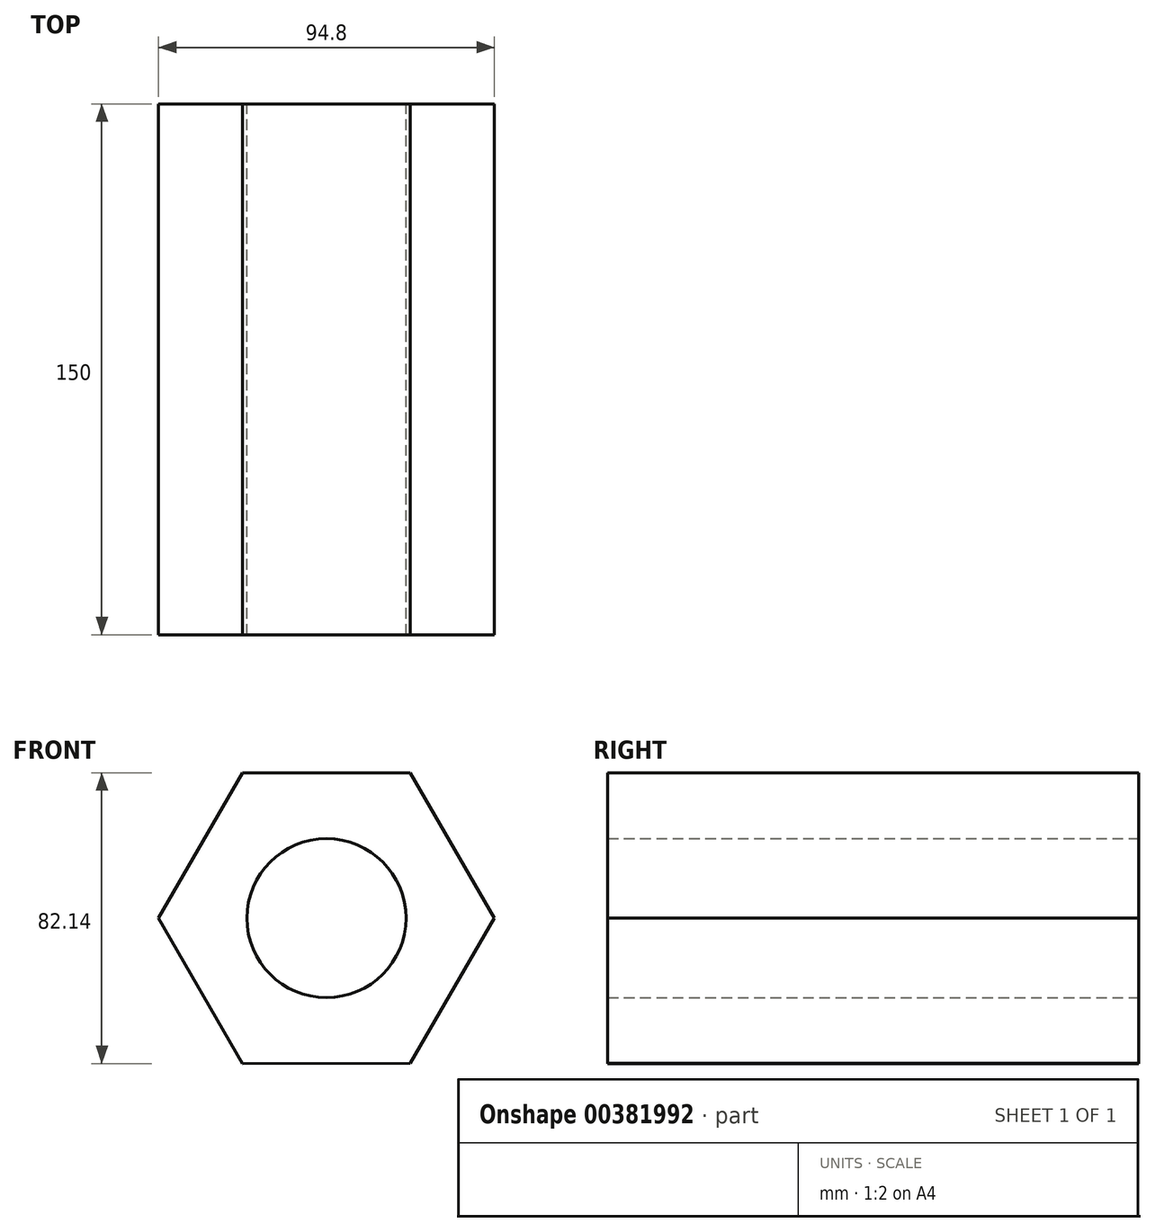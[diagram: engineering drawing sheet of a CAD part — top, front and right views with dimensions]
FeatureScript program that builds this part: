
annotation { "Feature Type Name" : "Feature", "Feature Type Description" : "" }
export const myFeature = defineFeature(function(context is Context, id is Id, definition is map)
    precondition{}
    {
        {
            var Q0;
            Q0=qCreatedBy(makeId("Front.planeOp"),FACE);
            var sketch = newSketch(context, id + "F0", { "sketchPlane" : qUnion([Q0])});
            skCircle(sketch, "E0.cCircle", {"center": v(0, 0) * mm, "radius": 41.05 * mm, "construction": true});
            skLineSegment(sketch, "E0.0", {"start": v(-47.4, -0.03) * mm, "end": v(-23.73, 41.04) * mm});
            skLineSegment(sketch, "E0.1", {"start": v(-23.73, 41.04) * mm, "end": v(23.68, 41.07) * mm});
            skLineSegment(sketch, "E0.2", {"start": v(23.68, 41.07) * mm, "end": v(47.4, 0.03) * mm});
            skLineSegment(sketch, "E0.3", {"start": v(47.4, 0.03) * mm, "end": v(23.73, -41.04) * mm});
            skLineSegment(sketch, "E0.4", {"start": v(23.73, -41.04) * mm, "end": v(-23.68, -41.07) * mm});
            skLineSegment(sketch, "E0.5", {"start": v(-23.68, -41.07) * mm, "end": v(-47.4, -0.03) * mm});
            skPoint(sketch, "E0.0.midPoint", {"position": v(-35.56, 20.5) * mm});
            skCircle(sketch, "E1", {"center": v(0, 0) * mm, "radius": 22.46 * mm});
            skSolve(sketch);
        }
        {
            var Q0;
            Q0 = qSketchRegion(id + "F0", true);
            extrude(context, id + "F1", {"entities" : qUnion([Q0]), "depth" : 150 * mm});
        }
    });
